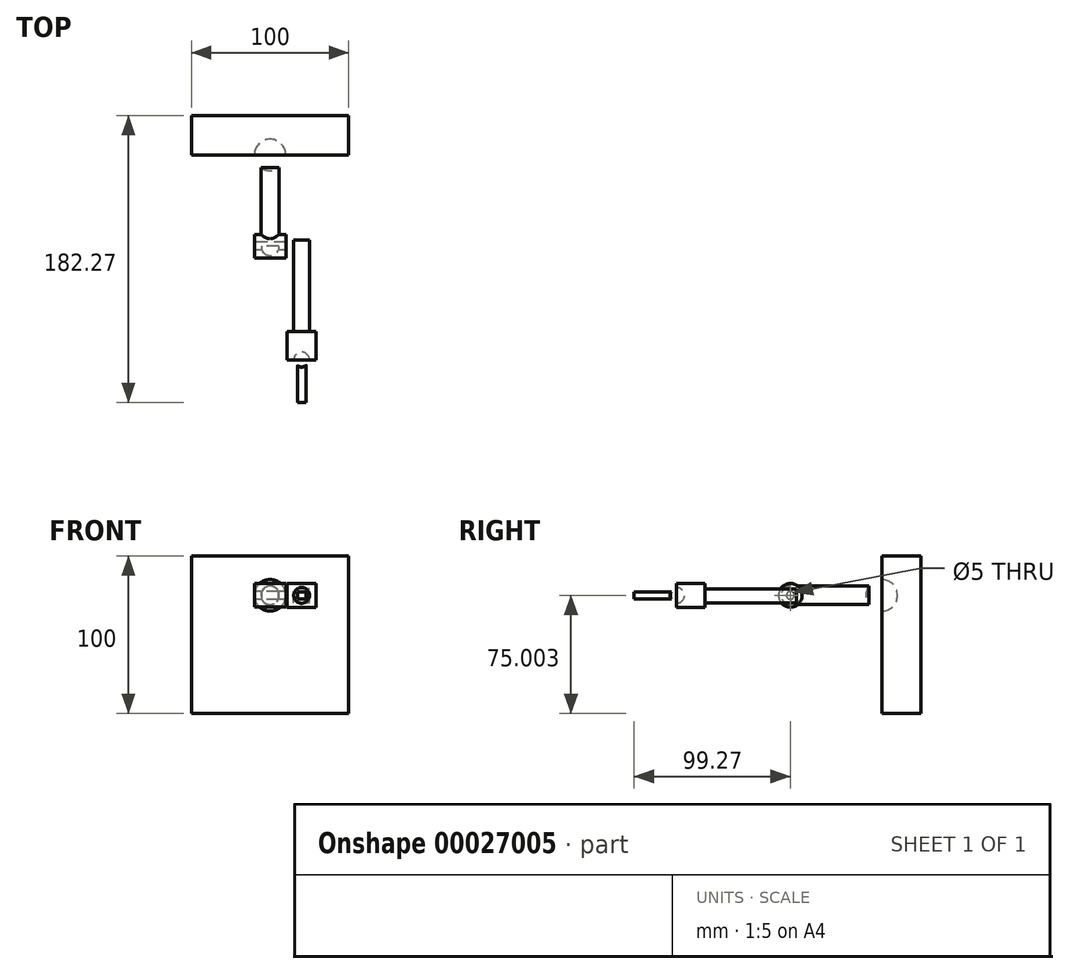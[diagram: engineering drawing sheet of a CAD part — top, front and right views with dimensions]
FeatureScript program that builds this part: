
annotation { "Feature Type Name" : "Feature", "Feature Type Description" : "" }
export const myFeature = defineFeature(function(context is Context, id is Id, definition is map)
    precondition{}
    {
        {
            var Q0;
            Q0=qCreatedBy(makeId("Front.planeOp"),FACE);
            var sketch = newSketch(context, id + "F0", { "sketchPlane" : qUnion([Q0])});
            skLineSegment(sketch, "E0.bottom", {"start": v(-46.72, 73.7) * mm, "end": v(53.28, 73.7) * mm});
            skLineSegment(sketch, "E0.top", {"start": v(-46.72, -26.3) * mm, "end": v(53.28, -26.3) * mm});
            skLineSegment(sketch, "E0.left", {"start": v(-46.72, 73.7) * mm, "end": v(-46.72, -26.3) * mm});
            skLineSegment(sketch, "E0.right", {"start": v(53.28, 73.7) * mm, "end": v(53.28, -26.3) * mm});
            skCircle(sketch, "E1", {"center": v(10.76, 10.87) * mm, "radius": 10 * mm});
            skSolve(sketch);
        }
        {
            var Q0;
            Q0=makeQuery(id+"F0.imprint","IMPRINT",FACE,{"disambiguationData":[TD([[makeQuery(id+"F0.imprint","IMPRINT",EDGE,{"derivedFrom":sQuery(id+"F0.wireOp",EDGE,"E0.bottom")}),-1.0]])]});
            var Q1;
            Q1=makeQuery(id+"F0.imprint","IMPRINT",FACE,{"disambiguationData":[TD([[makeQuery(id+"F0.imprint","IMPRINT",EDGE,{"derivedFrom":sQuery(id+"F0.wireOp",EDGE,"E1")}),1.0]])]});
            extrude(context, id + "F1", {"entities" : qUnion([Q0, Q1]), "depth" : 25 * mm});
        }
        {
            var Q0;
            Q0=makeQuery(id+"F1.opExtrude","CAP_FACE",FACE,{"disambiguationData":[OSD([sQuery(id+"F0.wireOp",EDGE,"E0.bottom"),sQuery(id+"F0.wireOp",EDGE,"E0.top"),sQuery(id+"F0.wireOp",EDGE,"E0.left"),sQuery(id+"F0.wireOp",EDGE,"E0.right")])],"isStart":false});
            var sketch = newSketch(context, id + "F2", { "sketchPlane" : qUnion([Q0])});
            skLineSegment(sketch, "E2.bottom", {"start": v(-46.72, 73.7) * mm, "end": v(53.28, 73.7) * mm});
            skLineSegment(sketch, "E2.top", {"start": v(-46.72, 48.7) * mm, "end": v(53.28, 48.7) * mm});
            skLineSegment(sketch, "E2.left", {"start": v(-46.72, 73.7) * mm, "end": v(-46.72, 48.7) * mm});
            skLineSegment(sketch, "E2.right", {"start": v(53.28, 73.7) * mm, "end": v(53.28, 48.7) * mm});
            skCircle(sketch, "E3", {"center": v(3.28, 48.7) * mm, "radius": 10 * mm});
            skSolve(sketch);
        }
        {
            var Q0;
            {var subQ0=sQuery(id+"F2.wireOp",EDGE,"E3");var subQ1=sQuery(id+"F2.wireOp",EDGE,"E2.top");var subQ3=makeQuery(id+"F2.imprint","INTERSECT",VERTEX,{"disambiguationData":[OD(0.0)],"derivedFrom":[subQ1,subQ0]});Q0=makeQuery(id+"F2.imprint","IMPRINT",FACE,{"disambiguationData":[TD([[makeQuery(id+"F2.imprint","IMPRINT",EDGE,{"disambiguationData":[TD([[subQ3,-1.0]])],"derivedFrom":subQ1}),1.0]])]});}
            var Q1;
            Q1=sQuery(id+"F2.wireOp",EDGE,"E2.top");
            revolve(context, id + "F3", {"entities" : qUnion([Q0]), "axis" : qUnion([Q1]), "revolveType" : RevolveType.FULL, "oppositeDirection" : true});
        }
        {
            var Q0;
            Q0=qCreatedBy(makeId("Front.planeOp"),FACE);
            cPlane(context, id + "F4", {"entities" : qUnion([Q0]), "cplaneType" : CPlaneType.OFFSET, "offset" : 35 * mm, "width" : 150 * mm, "height" : 150 * mm});
        }
        {
            var Q0;
            Q0=qCreatedBy(id+"F4.planeOp",FACE);
            var sketch = newSketch(context, id + "F5", { "sketchPlane" : qUnion([Q0])});
            skCircle(sketch, "E4", {"center": v(3.28, 48.7) * mm, "radius": 6.09 * mm});
            skSolve(sketch);
        }
        {
            var Q0;
            Q0=makeQuery(id+"F5.imprint","IMPRINT",FACE,{"disambiguationData":[TD([[makeQuery(id+"F5.imprint","IMPRINT",EDGE,{"derivedFrom":sQuery(id+"F5.wireOp",EDGE,"E4")}),1.0]])]});
            extrude(context, id + "F6", {"entities" : qUnion([Q0]), "operationType" : NewBodyOperationType.REMOVE, "oppositeDirection" : true, "depth" : 2 * mm});
        }
        {
            var Q0;
            Q0=makeQuery(id+"F6.boolean.opBoolean","COPY",FACE,{"derivedFrom":makeQuery(id+"F6.opExtrude","CAP_FACE",FACE,{"disambiguationData":[OSD([sQuery(id+"F5.wireOp",EDGE,"E4")])],"isStart":false})});
            var sketch = newSketch(context, id + "F7", { "sketchPlane" : qUnion([Q0])});
            skCircle(sketch, "E5", {"center": v(3.28, 48.7) * mm, "radius": 5.86 * mm});
            skSolve(sketch);
        }
        {
            var Q0;
            Q0=makeQuery(id+"F7.imprint","IMPRINT",FACE,{"disambiguationData":[TD([[makeQuery(id+"F7.imprint","IMPRINT",EDGE,{"derivedFrom":sQuery(id+"F7.wireOp",EDGE,"E5")}),1.0]])]});
            extrude(context, id + "F8", {"entities" : qUnion([Q0]), "operationType" : NewBodyOperationType.ADD, "depth" : 50 * mm});
        }
        {
            var Q0;
            Q0=makeQuery(id+"F8.opExtrude","CAP_FACE",FACE,{"disambiguationData":[OSD([sQuery(id+"F7.wireOp",EDGE,"E5")])],"isStart":false});
            var sketch = newSketch(context, id + "F9", { "sketchPlane" : qUnion([Q0])});
            skLineSegment(sketch, "E6.rect.bottom", {"start": v(13.28, 56.2) * mm, "end": v(-6.72, 56.2) * mm});
            skLineSegment(sketch, "E6.rect.top", {"start": v(13.28, 41.2) * mm, "end": v(-6.72, 41.2) * mm});
            skLineSegment(sketch, "E6.rect.left", {"start": v(13.28, 56.2) * mm, "end": v(13.28, 41.2) * mm});
            skLineSegment(sketch, "E6.rect.right", {"start": v(-6.72, 56.2) * mm, "end": v(-6.72, 41.2) * mm});
            skPoint(sketch, "E6.rect.middle", {"position": v(3.28, 48.7) * mm});
            skLineSegment(sketch, "E7", {"start": v(-6.72, 48.7) * mm, "end": v(13.28, 48.7) * mm});
            skSolve(sketch);
        }
        {
            var Q0;
            {var subQ8=sQuery(id+"F9.wireOp",EDGE,"E6.rect.bottom");Q0=makeQuery(id+"F9.imprint","IMPRINT",FACE,{"disambiguationData":[TD([[makeQuery(id+"F9.imprint","IMPRINT",EDGE,{"derivedFrom":subQ8}),1.0]])]});}
            var Q1;
            Q1=sQuery(id+"F9.wireOp",EDGE,"E7");
            revolve(context, id + "F10", {"operationType" : NewBodyOperationType.ADD, "entities" : qUnion([Q0]), "axis" : qUnion([Q1]), "revolveType" : RevolveType.FULL});
        }
        {
            var Q0;
            Q0=makeQuery(id+"F10.opRevolve","SWEPT_FACE",FACE,{"disambiguationData":[OSD([sQuery(id+"F9.wireOp",EDGE,"E6.rect.right")])]});
            var sketch = newSketch(context, id + "F11", { "sketchPlane" : qUnion([Q0])});
            skCircle(sketch, "E8", {"center": v(83, 48.7) * mm, "radius": 2.5 * mm});
            skSolve(sketch);
        }
        {
            var Q0;
            Q0=makeQuery(id+"F11.imprint","IMPRINT",FACE,{"disambiguationData":[TD([[makeQuery(id+"F11.imprint","IMPRINT",EDGE,{"derivedFrom":sQuery(id+"F11.wireOp",EDGE,"E8")}),1.0]])]});
            extrude(context, id + "F12", {"entities" : qUnion([Q0]), "oppositeDirection" : true, "depth" : 25 * mm});
        }
        {
            var Q0;
            Q0=makeQuery(id+"F12.opExtrude","CAP_FACE",FACE,{"disambiguationData":[OSD([sQuery(id+"F11.wireOp",EDGE,"E8")])],"isStart":false});
            var sketch = newSketch(context, id + "F13", { "sketchPlane" : qUnion([Q0])});
            skLineSegment(sketch, "E9.bottom", {"start": v(-78.99, 43.79) * mm, "end": v(-137.27, 43.79) * mm});
            skLineSegment(sketch, "E9.top", {"start": v(-78.99, 52.85) * mm, "end": v(-137.27, 52.85) * mm});
            skLineSegment(sketch, "E9.left", {"start": v(-78.99, 43.79) * mm, "end": v(-78.99, 52.85) * mm});
            skLineSegment(sketch, "E9.right", {"start": v(-137.27, 43.79) * mm, "end": v(-137.27, 52.85) * mm});
            skSolve(sketch);
        }
        {
            var Q0;
            Q0=makeQuery(id+"F13.imprint","IMPRINT",FACE,{"disambiguationData":[TD([[makeQuery(id+"F13.imprint","IMPRINT",EDGE,{"derivedFrom":makeQuery(id+"F12.opExtrude","CAP_EDGE",EDGE,{"disambiguationData":[OSD([sQuery(id+"F11.wireOp",EDGE,"E8")])],"isStart":false})}),-1.0]])]});
            var Q1;
            Q1=makeQuery(id+"F13.imprint","IMPRINT",FACE,{"disambiguationData":[TD([[makeQuery(id+"F13.imprint","IMPRINT",EDGE,{"derivedFrom":sQuery(id+"F13.wireOp",EDGE,"E9.bottom")}),-1.0]])]});
            extrude(context, id + "F14", {"entities" : qUnion([Q0, Q1]), "operationType" : NewBodyOperationType.ADD, "depth" : 10 * mm});
        }
        {
            var Q0;
            Q0=makeQuery(id+"F14.opExtrude","SWEPT_FACE",FACE,{"disambiguationData":[OSD([sQuery(id+"F13.wireOp",EDGE,"E9.right")])]});
            var sketch = newSketch(context, id + "F15", { "sketchPlane" : qUnion([Q0])});
            skLineSegment(sketch, "E10.bottom", {"start": v(14.1, 56.3) * mm, "end": v(32.57, 56.3) * mm});
            skLineSegment(sketch, "E10.top", {"start": v(14.1, 41.01) * mm, "end": v(32.57, 41.01) * mm});
            skLineSegment(sketch, "E10.left", {"start": v(14.1, 56.3) * mm, "end": v(14.1, 41.01) * mm});
            skLineSegment(sketch, "E10.right", {"start": v(32.57, 56.3) * mm, "end": v(32.57, 41.01) * mm});
            skSolve(sketch);
        }
        {
            var Q0;
            {var subQ0=sQuery(id+"F13.wireOp",EDGE,"E9.right");Q0=makeQuery(id+"F15.imprint","IMPRINT",FACE,{"disambiguationData":[TD([[makeQuery(id+"F15.imprint","IMPRINT",EDGE,{"derivedFrom":makeQuery(id+"F14.opExtrude","CAP_EDGE",EDGE,{"disambiguationData":[OSD([subQ0])],"isStart":true})}),-1.0]])]});}
            var Q1;
            Q1=makeQuery(id+"F15.imprint","IMPRINT",FACE,{"disambiguationData":[TD([[makeQuery(id+"F15.imprint","IMPRINT",EDGE,{"derivedFrom":sQuery(id+"F15.wireOp",EDGE,"E10.bottom")}),-1.0]])]});
            extrude(context, id + "F16", {"entities" : qUnion([Q0, Q1]), "operationType" : NewBodyOperationType.ADD, "depth" : 18 * mm});
        }
        {
            var Q0;
            Q0=makeQuery(id+"F16.opExtrude","CAP_FACE",FACE,{"disambiguationData":[OSD([sQuery(id+"F15.wireOp",EDGE,"E10.bottom"),sQuery(id+"F15.wireOp",EDGE,"E10.top"),sQuery(id+"F15.wireOp",EDGE,"E10.left"),sQuery(id+"F15.wireOp",EDGE,"E10.right")])],"isStart":false});
            var sketch = newSketch(context, id + "F17", { "sketchPlane" : qUnion([Q0])});
            skLineSegment(sketch, "E11", {"start": v(14.1, 48.66) * mm, "end": v(32.57, 48.66) * mm});
            skCircle(sketch, "E12", {"center": v(23.34, 48.66) * mm, "radius": 5 * mm});
            skSolve(sketch);
        }
        {
            var Q0;
            {var subQ0=sQuery(id+"F17.wireOp",EDGE,"E12");var subQ1=sQuery(id+"F17.wireOp",EDGE,"E11");var subQ3=makeQuery(id+"F17.imprint","INTERSECT",VERTEX,{"disambiguationData":[OD(0.0)],"derivedFrom":[subQ1,subQ0]});Q0=makeQuery(id+"F17.imprint","IMPRINT",FACE,{"disambiguationData":[TD([[makeQuery(id+"F17.imprint","IMPRINT",EDGE,{"disambiguationData":[TD([[subQ3,-1.0]])],"derivedFrom":subQ1}),1.0]])]});}
            var Q1;
            Q1=sQuery(id+"F17.wireOp",EDGE,"E11");
            revolve(context, id + "F18", {"entities" : qUnion([Q0]), "axis" : qUnion([Q1]), "revolveType" : RevolveType.FULL, "oppositeDirection" : true});
        }
        {
            var Q0;
            Q0=makeQuery(id+"F16.opExtrude","CAP_FACE",FACE,{"disambiguationData":[OSD([sQuery(id+"F15.wireOp",EDGE,"E10.bottom"),sQuery(id+"F15.wireOp",EDGE,"E10.top"),sQuery(id+"F15.wireOp",EDGE,"E10.left"),sQuery(id+"F15.wireOp",EDGE,"E10.right")])],"isStart":false});
            cPlane(context, id + "F19", {"entities" : qUnion([Q0]), "cplaneType" : CPlaneType.OFFSET, "offset" : 5 * mm, "width" : 150 * mm, "height" : 150 * mm});
        }
        {
            var Q0;
            Q0=qCreatedBy(id+"F19.planeOp",FACE);
            var sketch = newSketch(context, id + "F20", { "sketchPlane" : qUnion([Q0])});
            skLineSegment(sketch, "E13.bottom", {"start": v(20.7, 50.8) * mm, "end": v(26.3, 50.8) * mm});
            skLineSegment(sketch, "E13.top", {"start": v(20.7, 46.32) * mm, "end": v(26.3, 46.32) * mm});
            skLineSegment(sketch, "E13.left", {"start": v(20.7, 50.8) * mm, "end": v(20.7, 46.32) * mm});
            skLineSegment(sketch, "E13.right", {"start": v(26.3, 50.8) * mm, "end": v(26.3, 46.32) * mm});
            skSolve(sketch);
        }
        {
            var Q0;
            Q0=makeQuery(id+"F20.imprint","IMPRINT",FACE,{"disambiguationData":[TD([[makeQuery(id+"F20.imprint","IMPRINT",EDGE,{"derivedFrom":sQuery(id+"F20.wireOp",EDGE,"E13.bottom")}),-1.0]])]});
            extrude(context, id + "F21", {"entities" : qUnion([Q0]), "operationType" : NewBodyOperationType.REMOVE, "oppositeDirection" : true, "depth" : 3 * mm});
        }
        {
            var Q0;
            Q0=makeQuery(id+"F21.boolean.opBoolean","COPY",FACE,{"derivedFrom":makeQuery(id+"F21.opExtrude","CAP_FACE",FACE,{"disambiguationData":[OSD([sQuery(id+"F20.wireOp",EDGE,"E13.bottom"),sQuery(id+"F20.wireOp",EDGE,"E13.top"),sQuery(id+"F20.wireOp",EDGE,"E13.left"),sQuery(id+"F20.wireOp",EDGE,"E13.right")])],"isStart":false})});
            var sketch = newSketch(context, id + "F22", { "sketchPlane" : qUnion([Q0])});
            skLineSegment(sketch, "E14.bottom", {"start": v(20.7, 50.8) * mm, "end": v(26.3, 50.8) * mm});
            skLineSegment(sketch, "E14.top", {"start": v(20.7, 46.32) * mm, "end": v(26.3, 46.32) * mm});
            skLineSegment(sketch, "E14.left", {"start": v(20.7, 50.8) * mm, "end": v(20.7, 46.32) * mm});
            skLineSegment(sketch, "E14.right", {"start": v(26.3, 50.8) * mm, "end": v(26.3, 46.32) * mm});
            skSolve(sketch);
        }
        {
            var Q0;
            Q0=makeQuery(id+"F22.imprint","IMPRINT",FACE,{"disambiguationData":[TD([[makeQuery(id+"F22.imprint","IMPRINT",EDGE,{"derivedFrom":sQuery(id+"F22.wireOp",EDGE,"E14.bottom")}),-1.0]])]});
            extrude(context, id + "F23", {"entities" : qUnion([Q0]), "operationType" : NewBodyOperationType.ADD, "depth" : 25 * mm});
        }
        {
            var Q0;
            {var subQ0=sQuery(id+"F2.wireOp",EDGE,"E3");var subQ1=sQuery(id+"F2.wireOp",EDGE,"E2.top");var subQ3=makeQuery(id+"F2.imprint","INTERSECT",VERTEX,{"disambiguationData":[OD(0.0)],"derivedFrom":[subQ1,subQ0]});Q0=makeQuery(id+"F2.imprint","IMPRINT",FACE,{"disambiguationData":[TD([[makeQuery(id+"F2.imprint","IMPRINT",EDGE,{"disambiguationData":[TD([[subQ3,-1.0]])],"derivedFrom":subQ1}),1.0]])]});}
            var Q1;
            Q1=sQuery(id+"F2.wireOp",EDGE,"E2.top");
            revolve(context, id + "F24", {"operationType" : NewBodyOperationType.REMOVE, "entities" : qUnion([Q0]), "axis" : qUnion([Q1]), "revolveType" : RevolveType.FULL, "oppositeDirection" : true});
        }
        {
            var Q0;
            Q0=makeQuery(id+"F11.imprint","IMPRINT",FACE,{"disambiguationData":[TD([[makeQuery(id+"F11.imprint","IMPRINT",EDGE,{"derivedFrom":sQuery(id+"F11.wireOp",EDGE,"E8")}),1.0]])]});
            extrude(context, id + "F25", {"entities" : qUnion([Q0]), "operationType" : NewBodyOperationType.REMOVE, "oppositeDirection" : true, "depth" : 25 * mm});
        }
        {
            var Q0;
            {var subQ0=sQuery(id+"F17.wireOp",EDGE,"E12");var subQ1=sQuery(id+"F17.wireOp",EDGE,"E11");var subQ3=makeQuery(id+"F17.imprint","INTERSECT",VERTEX,{"disambiguationData":[OD(0.0)],"derivedFrom":[subQ1,subQ0]});Q0=makeQuery(id+"F17.imprint","IMPRINT",FACE,{"disambiguationData":[TD([[makeQuery(id+"F17.imprint","IMPRINT",EDGE,{"disambiguationData":[TD([[subQ3,-1.0]])],"derivedFrom":subQ1}),-1.0]])]});}
            var Q1;
            Q1=sQuery(id+"F17.wireOp",EDGE,"E11");
            revolve(context, id + "F26", {"operationType" : NewBodyOperationType.REMOVE, "entities" : qUnion([Q0]), "axis" : qUnion([Q1]), "revolveType" : RevolveType.FULL, "oppositeDirection" : true});
        }
    });
